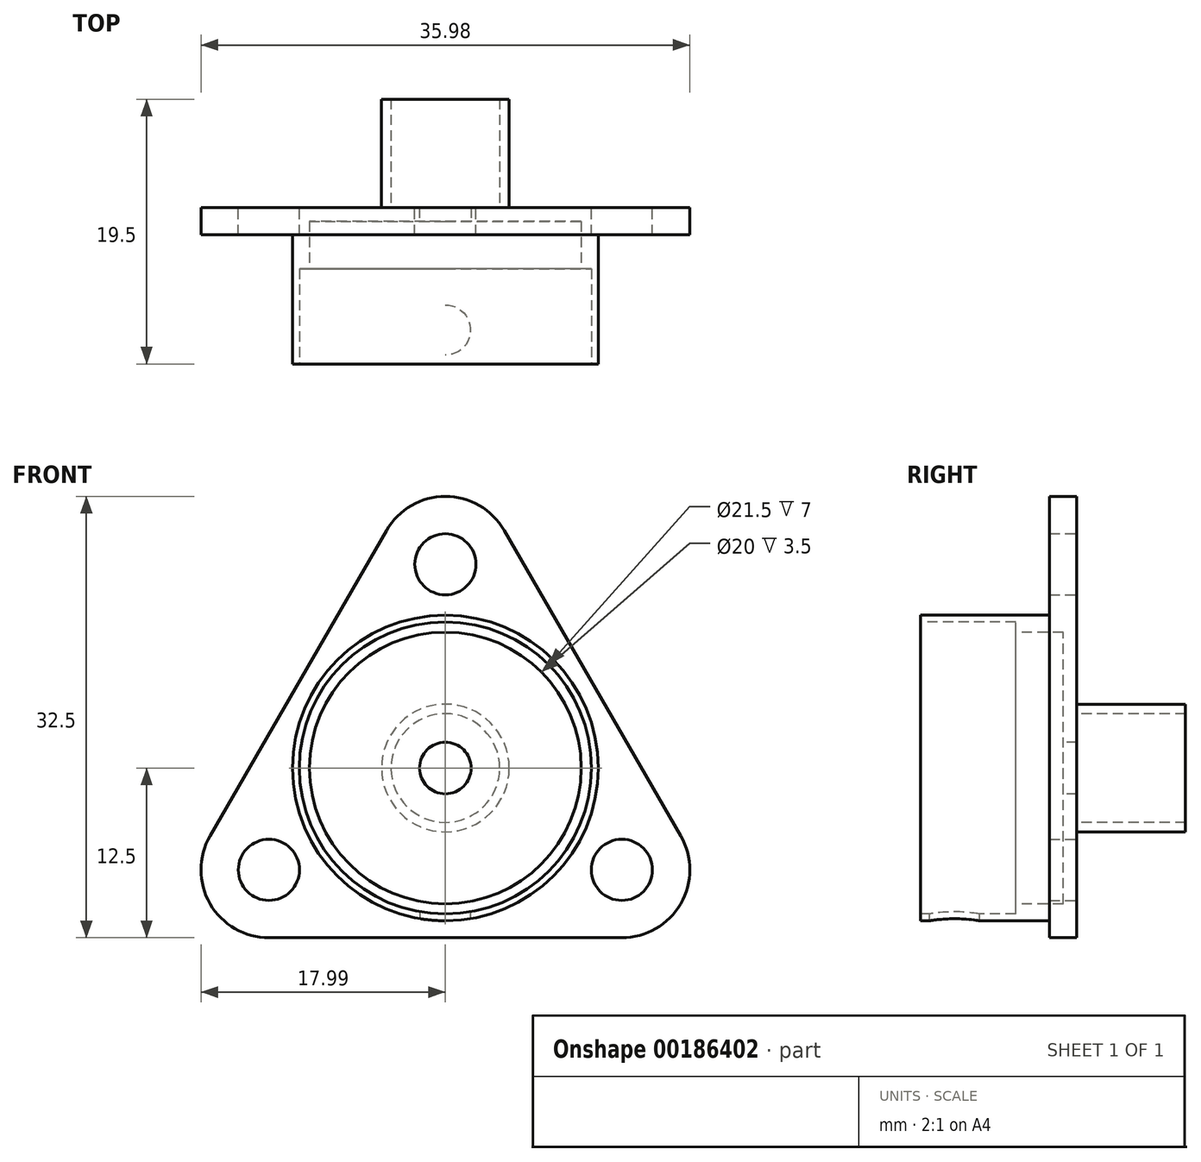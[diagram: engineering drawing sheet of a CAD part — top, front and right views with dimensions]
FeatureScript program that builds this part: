
annotation { "Feature Type Name" : "Feature", "Feature Type Description" : "" }
export const myFeature = defineFeature(function(context is Context, id is Id, definition is map)
    precondition{}
    {
        {
            var Q0;
            Q0=qCreatedBy(makeId("Right.planeOp"),FACE);
            var sketch = newSketch(context, id + "F0", { "sketchPlane" : qUnion([Q0])});
            skLineSegment(sketch, "E0", {"start": v(0, 0) * mm, "end": v(26.9, 0) * mm, "construction": true});
            skLineSegment(sketch, "E1", {"start": v(0, 11.25) * mm, "end": v(11.5, 11.25) * mm});
            skLineSegment(sketch, "E2", {"start": v(11.5, 11.25) * mm, "end": v(11.5, 4.7) * mm});
            skLineSegment(sketch, "E3", {"start": v(11.5, 4.7) * mm, "end": v(19.5, 4.7) * mm});
            skLineSegment(sketch, "E4", {"start": v(19.5, 4.7) * mm, "end": v(19.5, 4) * mm});
            skLineSegment(sketch, "E5", {"start": v(19.5, 4) * mm, "end": v(11.5, 4) * mm});
            skLineSegment(sketch, "E6", {"start": v(11.5, 4) * mm, "end": v(11.5, 1.9) * mm});
            skLineSegment(sketch, "E7", {"start": v(11.5, 1.9) * mm, "end": v(10.5, 1.9) * mm});
            skLineSegment(sketch, "E8", {"start": v(10.5, 1.9) * mm, "end": v(10.5, 10) * mm});
            skLineSegment(sketch, "E9", {"start": v(10.5, 10) * mm, "end": v(7, 10) * mm});
            skLineSegment(sketch, "E10", {"start": v(7, 10) * mm, "end": v(7, 10.75) * mm});
            skLineSegment(sketch, "E11", {"start": v(7, 10.75) * mm, "end": v(0, 10.75) * mm});
            skLineSegment(sketch, "E12", {"start": v(0, 10.75) * mm, "end": v(0, 11.25) * mm});
            skSolve(sketch);
        }
        {
            var Q0;
            Q0=makeQuery(id+"F0.imprint","IMPRINT",FACE,{"disambiguationData":[TD([[makeQuery(id+"F0.imprint","IMPRINT",EDGE,{"derivedFrom":sQuery(id+"F0.wireOp",EDGE,"E1")}),-1.0]])]});
            var Q1;
            Q1=sQuery(id+"F0.wireOp",EDGE,"E0");
            revolve(context, id + "F1", {"entities" : qUnion([Q0]), "axis" : qUnion([Q1]), "revolveType" : RevolveType.FULL});
        }
        {
            var Q0;
            Q0=qCreatedBy(makeId("Top.planeOp"),FACE);
            var sketch = newSketch(context, id + "F2", { "sketchPlane" : qUnion([Q0])});
            skCircle(sketch, "E13", {"center": v(0, 2.5) * mm, "radius": 1.85 * mm});
            skSolve(sketch);
        }
        {
            var Q0;
            Q0=makeQuery(id+"F2.imprint","IMPRINT",FACE,{"disambiguationData":[TD([[makeQuery(id+"F2.imprint","IMPRINT",EDGE,{"derivedFrom":sQuery(id+"F2.wireOp",EDGE,"E13")}),1.0]])]});
            extrude(context, id + "F3", {"entities" : qUnion([Q0]), "operationType" : NewBodyOperationType.REMOVE, "endBound" : BoundingType.THROUGH_ALL, "oppositeDirection" : true, "depth" : 25 * mm});
        }
        {
            var Q0;
            Q0=makeQuery(id+"F1.opRevolve","SWEPT_FACE",FACE,{"disambiguationData":[OSD([sQuery(id+"F0.wireOp",EDGE,"E2")])]});
            var sketch = newSketch(context, id + "F4", { "sketchPlane" : qUnion([Q0])});
            skCircle(sketch, "E14", {"center": v(0, 0) * mm, "radius": 15 * mm, "construction": true});
            skLineSegment(sketch, "E15.0", {"start": v(4.33, 17.5) * mm, "end": v(17.32, -5) * mm});
            skLineSegment(sketch, "E15.1", {"start": v(13, -12.5) * mm, "end": v(-13, -12.5) * mm});
            skLineSegment(sketch, "E15.2", {"start": v(-17.32, -5) * mm, "end": v(-4.33, 17.5) * mm});
            skPoint(sketch, "E16.visualSharp", {"position": v(0, 25) * mm});
            skArc(sketch, "E16.filletArc", {"start": v(4.33, 17.5) * mm, "mid": v(0, 20) * mm, "end": v(-4.33, 17.5) * mm});
            skPoint(sketch, "E17.visualSharp", {"position": v(-21.65, -12.5) * mm});
            skArc(sketch, "E17.filletArc", {"start": v(-17.32, -5) * mm, "mid": v(-17.32, -10) * mm, "end": v(-13, -12.5) * mm});
            skPoint(sketch, "E18.visualSharp", {"position": v(21.65, -12.5) * mm});
            skArc(sketch, "E18.filletArc", {"start": v(13, -12.5) * mm, "mid": v(17.32, -10) * mm, "end": v(17.32, -5) * mm});
            skCircle(sketch, "E19", {"center": v(0, 15) * mm, "radius": 2.25 * mm});
            skCircle(sketch, "E20", {"center": v(-13, -7.5) * mm, "radius": 2.25 * mm});
            skCircle(sketch, "E21", {"center": v(13, -7.5) * mm, "radius": 2.25 * mm});
            skCircle(sketch, "E22.0", {"center": v(0, 0) * mm, "radius": 10.75 * mm});
            skSolve(sketch);
        }
        {
            var Q0;
            Q0=makeQuery(id+"F4.imprint","IMPRINT",FACE,{"disambiguationData":[TD([[makeQuery(id+"F4.imprint","IMPRINT",EDGE,{"derivedFrom":sQuery(id+"F4.wireOp",EDGE,"E15.0")}),-1.0]])]});
            var Q1;
            Q1=makeQuery(id+"F4.imprint","IMPRINT",FACE,{"disambiguationData":[TD([[makeQuery(id+"F4.imprint","IMPRINT",EDGE,{"derivedFrom":sQuery(id+"F4.wireOp",EDGE,"E22.0")}),-1.0]])]});
            extrude(context, id + "F5", {"entities" : qUnion([Q0, Q1]), "operationType" : NewBodyOperationType.ADD, "oppositeDirection" : true, "depth" : 2 * mm});
        }
    });
